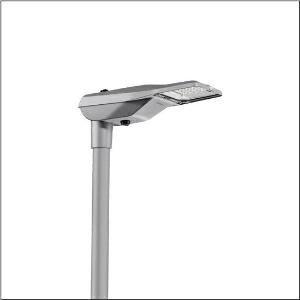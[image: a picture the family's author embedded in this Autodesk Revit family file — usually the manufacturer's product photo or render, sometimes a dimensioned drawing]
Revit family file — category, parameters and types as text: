
# Revit family: streetlight_sl_21_micro___st0_8a_5xe1c43t08db_13be
name_source: partatom
category: Lighting Fixtures
units: mm (PartAtom-declared; Revit-internal decimal feet)

## family parameters
Cut with Voids When Loaded = No
Host = Face
Light Source = No
Part Type = Normal
Room Calculation Point = No
Round Connector Dimension = Use Diameter
Shared = No

## types (1)
- --- (1 x LED, 5320 lm, 39.1 W, 4000K)
    Apparent Load = 39 VA
    CIE Flux Codes = 38 75 97 100 100
    Color Rendering = 70
    Color Temperature = 4000K
    Default Elevation = 1800 mm
    Description = Streetlight SL 21 micro, mast luminaire, primary light control with lens, of PMMA, primary optical cover: cover, of toughened safety glass, transparent, light distribution: ST0.8a, light emission: direct distribution, primary light characteristic: asymmetric, installation type: side-entry, post-top, LED, High Power LED, rated luminous flux: 5.320lm, luminous efficacy: 136lm/W, light colour: 740, colour temperature: 4000K, control: flexible luminous flux parameterisation, time-dependent luminous flux control, constant luminous flux control, overheat protection, presetting dimming logarithmic, mains connection: 220..240V, AC, 50/60Hz, start of lifetime: 39W, end of service life: 41W, reduction: 18W, luminaire housing, of diecast aluminium, powder-coated, Siteco® metallic grey (DB 702S), corrosivity category C5 mid according to DIN EN ISO 12944, please order mast flange separately, inclination adjustable: 0°, 5°, 10°, 15°, sealing non-destructively replaceable, multi-level sealing system, length: 528mm, width: 235mm, height: 110mm, mast flange for spigot size: 42mm (side-entry): 5XC10008XM4, 60/48mm (side-entry/post-top): 5XC10108XM2, 76/60mm (side-entry/post-top): 5XC10108XM1, Smart Interface below and above, protection rating (complete): IP66, insulation class (complete): insulation class II (safety insulation), certification: CE, ENEC, ENEC+, VDE, impact resistance: IK09, permissible operating ambient temperature for outdoor applications: -40..+50°C, standard-compliant lighting for roads and squares, packaging unit: 1 piece

Light Distribution: ST0.8a
    Height = 110 mm
    Lamp = 1 x LED
    Lamp Light Flux = 5320 lm
    Lamp Power = 39.1 W
    Lamp count = 1
    Length = 528 mm
    Luminous efficacy = 136 lm/W
    Manufacturer = Siteco
    ModVariant = No
    Model = 5XE1C43T08DB
    Number of Poles = 1
    OnlyDefault = Yes
    Power Factor = 1
    Product Name = Streetlight SL 21 micro | ST0.8a
    Product group = mast luminaire | pylon top
    ProductGroupID = 6100
    Protection Class = Protection class II
    Protection Degree = IP 66
    RLX_Detail_Level = 1
    RLX_Emergency_Light_Flux = 0 lm
    RLX_Emergency_Type = 0
    RLX_Emergency_Type_DB = No
    RlxData = <blob elided: 98997 chars, md5=2ee900fe>
    Socket = socket
    Standby Power = 0 W
    System Light Flux = 5320 lm
    System Power = 39 W
    Type Comments = factory setting: luminous flux: 100 % | dim-lin: 254 | 765 mA
    Type Image = l_1007239.jpg
    URL = http://relux.com
    VarID = @adj_104469
    Voltage = 0 V
    Weight = 0.00 kg
    Width = 235 mm

## geometry (parser evidence)
native form markers: Blend x4, Sweep x10
no freeform markers — native parametric forms only
